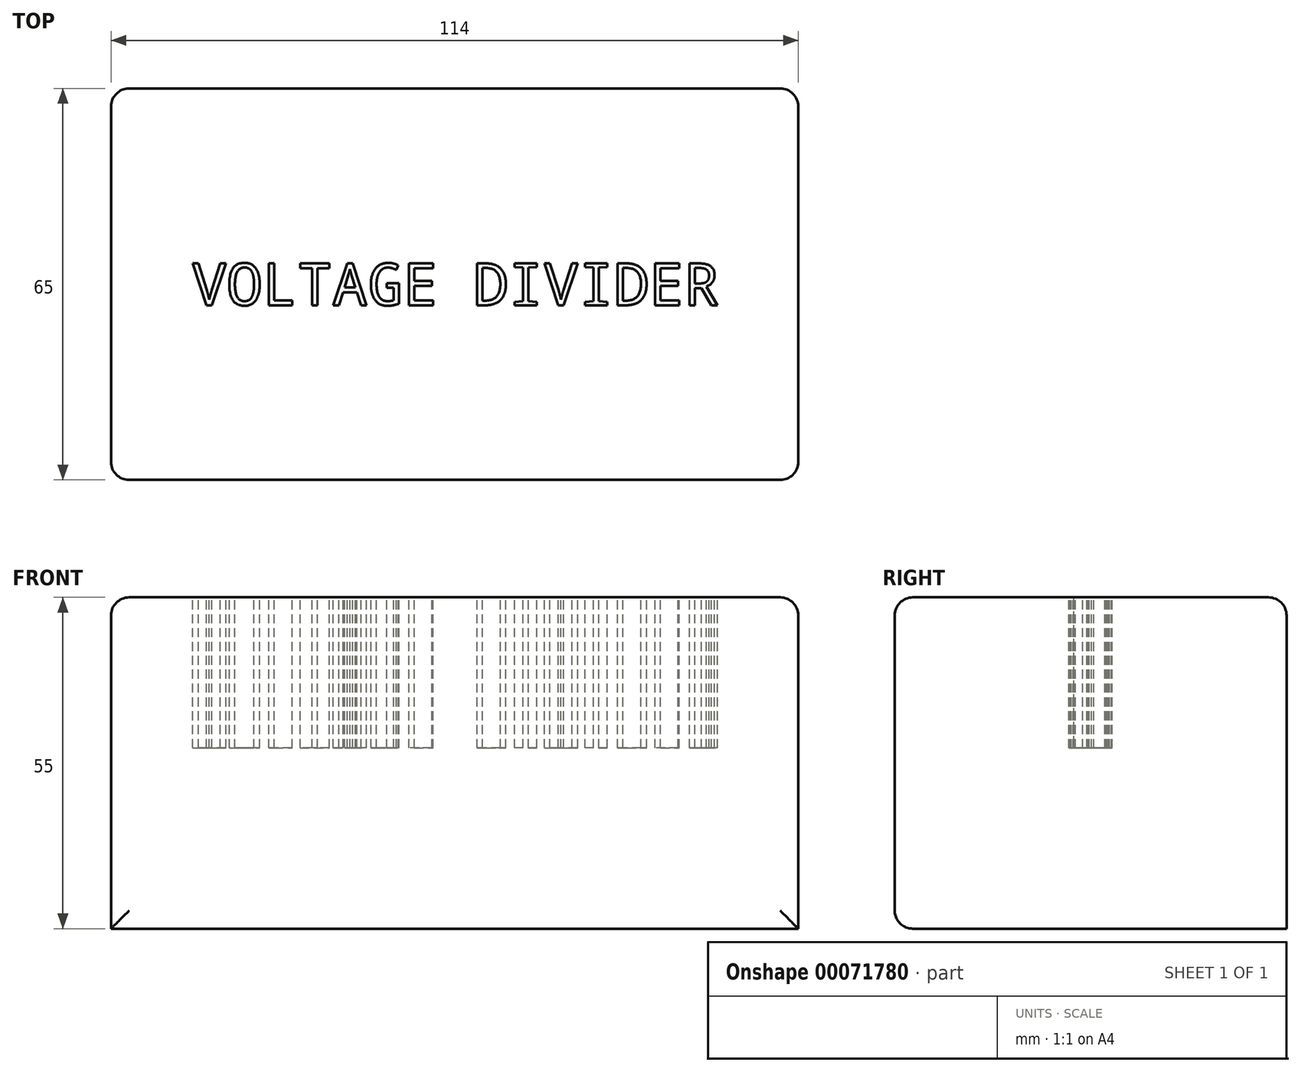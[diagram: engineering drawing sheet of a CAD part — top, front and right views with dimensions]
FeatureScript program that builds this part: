
annotation { "Feature Type Name" : "Feature", "Feature Type Description" : "" }
export const myFeature = defineFeature(function(context is Context, id is Id, definition is map)
    precondition{}
    {
        {
            var Q0;
            Q0=qCreatedBy(makeId("Top.planeOp"),FACE);
            var sketch = newSketch(context, id + "F0", { "sketchPlane" : qUnion([Q0])});
            skLineSegment(sketch, "E0.rect.bottom", {"start": v(57, -32.5) * mm, "end": v(-57, -32.5) * mm});
            skLineSegment(sketch, "E0.rect.top", {"start": v(57, 32.5) * mm, "end": v(-57, 32.5) * mm});
            skLineSegment(sketch, "E0.rect.left", {"start": v(57, -32.5) * mm, "end": v(57, 32.5) * mm});
            skLineSegment(sketch, "E0.rect.right", {"start": v(-57, -32.5) * mm, "end": v(-57, 32.5) * mm});
            skPoint(sketch, "E0.rect.middle", {"position": v(0, 0) * mm});
            skSolve(sketch);
        }
        {
            var Q0;
            Q0 = qSketchRegion(id + "F0", true);
            extrude(context, id + "F1", {"entities" : qUnion([Q0]), "depth" : 55 * mm});
        }
        {
            var Q0;
            Q0=makeQuery(id+"F1.opExtrude","CAP_FACE",FACE,{"disambiguationData":[OSD([sQuery(id+"F0.wireOp",EDGE,"E0.rect.bottom"),sQuery(id+"F0.wireOp",EDGE,"E0.rect.top"),sQuery(id+"F0.wireOp",EDGE,"E0.rect.left"),sQuery(id+"F0.wireOp",EDGE,"E0.rect.right")])],"isStart":false});
            var sketch = newSketch(context, id + "F2", { "sketchPlane" : qUnion([Q0])});
            skText(sketch, "E1", { "text": "VOLTAGE DIVIDER", "fontName": "DroidSansMono.ttf"});
            const initialGuessF2  = {"E1": [-0.04362, -0.0035, 1, 0, 0.007]};
            skSetInitialGuess(sketch, initialGuessF2);
            skSolve(sketch);
        }
        {
            var Q0;
            Q0 = qSketchRegion(id + "F2", true);
            extrude(context, id + "F3", {"entities" : qUnion([Q0]), "operationType" : NewBodyOperationType.REMOVE, "oppositeDirection" : true, "depth" : 25 * mm});
        }
        {
            var Q0;
            Q0=makeQuery(id+"F1.opExtrude","CAP_EDGE",EDGE,{"disambiguationData":[OSD([sQuery(id+"F0.wireOp",EDGE,"E0.rect.left")])],"isStart":false});
            var Q1;
            Q1=makeQuery(id+"F1.opExtrude","CAP_EDGE",EDGE,{"disambiguationData":[OSD([sQuery(id+"F0.wireOp",EDGE,"E0.rect.bottom")])],"isStart":false});
            var Q2;
            Q2=makeQuery(id+"F1.opExtrude","SWEPT_EDGE",EDGE,{"disambiguationData":[OSD([sQuery(id+"F0.wireOp",EDGE,"E0.rect.bottom"),sQuery(id+"F0.wireOp",EDGE,"E0.rect.left")])]});
            var Q3;
            Q3=makeQuery(id+"F1.opExtrude","CAP_EDGE",EDGE,{"disambiguationData":[OSD([sQuery(id+"F0.wireOp",EDGE,"E0.rect.right")])],"isStart":false});
            var Q4;
            Q4=makeQuery(id+"F1.opExtrude","CAP_EDGE",EDGE,{"disambiguationData":[OSD([sQuery(id+"F0.wireOp",EDGE,"E0.rect.top")])],"isStart":false});
            var Q5;
            Q5=makeQuery(id+"F1.opExtrude","SWEPT_FACE",FACE,{"disambiguationData":[OSD([sQuery(id+"F0.wireOp",EDGE,"E0.rect.bottom")])]});
            var Q6;
            Q6=makeQuery(id+"F1.opExtrude","SWEPT_EDGE",EDGE,{"disambiguationData":[OSD([sQuery(id+"F0.wireOp",EDGE,"E0.rect.top"),sQuery(id+"F0.wireOp",EDGE,"E0.rect.right")])]});
            var Q7;
            Q7=makeQuery(id+"F1.opExtrude","SWEPT_EDGE",EDGE,{"disambiguationData":[OSD([sQuery(id+"F0.wireOp",EDGE,"E0.rect.top"),sQuery(id+"F0.wireOp",EDGE,"E0.rect.left")])]});
            fillet(context, id + "F4", {"entities" : qUnion([Q0, Q1, Q2, Q3, Q4, Q5, Q6, Q7]), "radius" : 3 * mm, "tangentPropagation" : true, "allowEdgeOverflow" : false});
        }
    });
